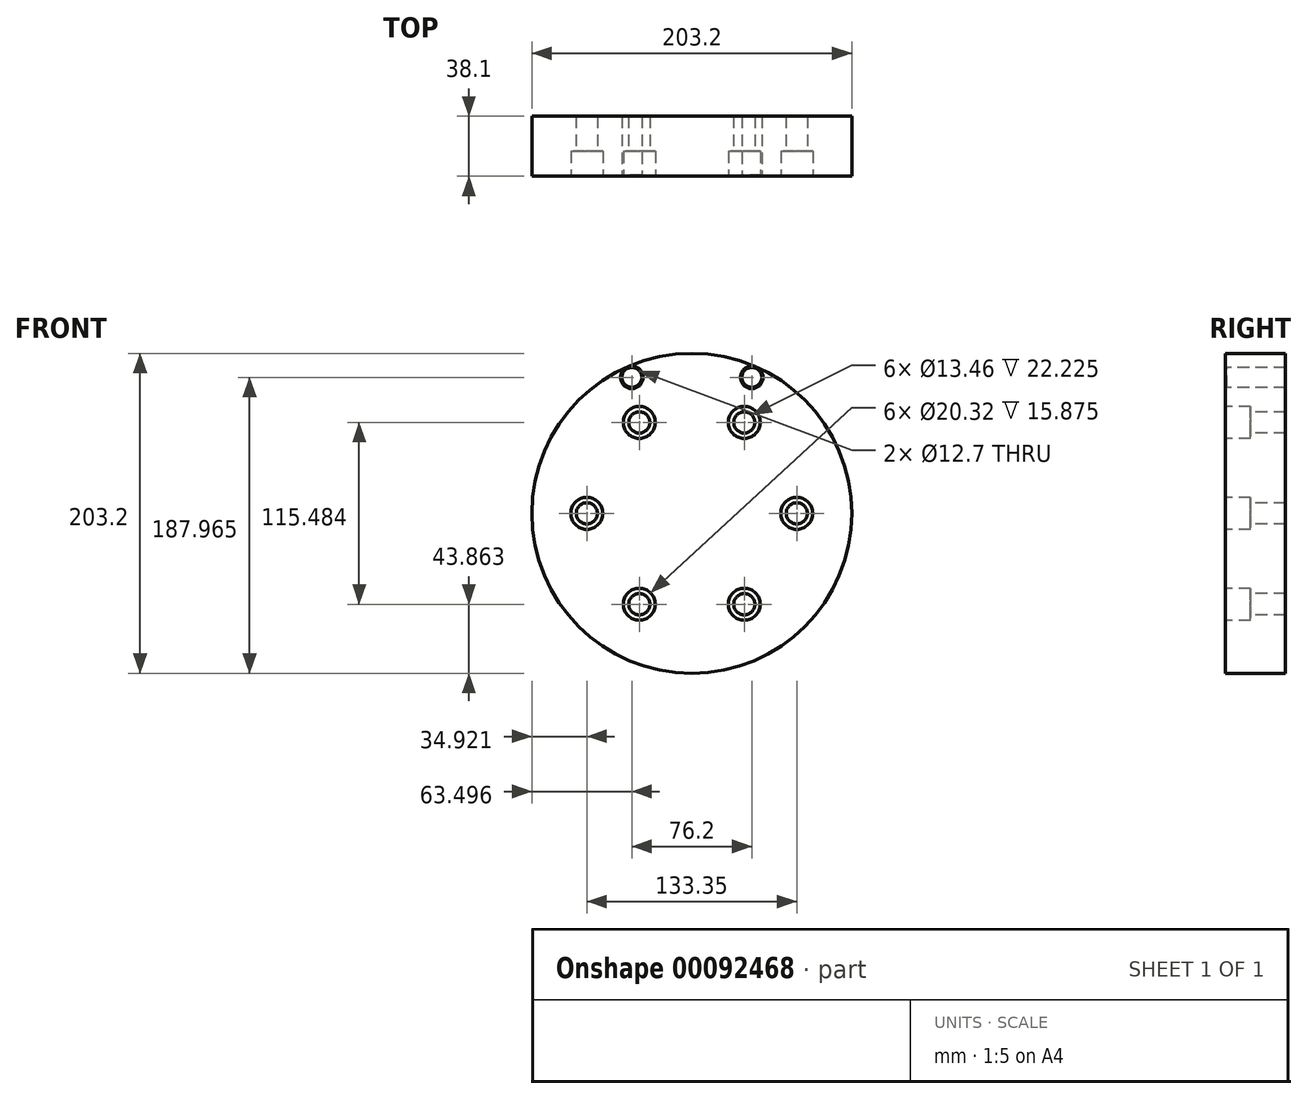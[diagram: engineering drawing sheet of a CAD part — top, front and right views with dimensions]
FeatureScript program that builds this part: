
annotation { "Feature Type Name" : "Feature", "Feature Type Description" : "" }
export const myFeature = defineFeature(function(context is Context, id is Id, definition is map)
    precondition{}
    {
        {
            var Q0;
            Q0=qCreatedBy(makeId("Front.planeOp"),FACE);
            var sketch = newSketch(context, id + "F0", { "sketchPlane" : qUnion([Q0])});
            skCircle(sketch, "E0", {"center": v(0, 0) * mm, "radius": 101.6 * mm});
            skPoint(sketch, "E1", {"position": v(0, 66.68) * mm});
            skPoint(sketch, "E2.1.0", {"position": v(-57.74, 33.34) * mm});
            skPoint(sketch, "E2.2.0", {"position": v(-57.74, -33.34) * mm});
            skPoint(sketch, "E2.3.0", {"position": v(0, -66.68) * mm});
            skPoint(sketch, "E2.4.0", {"position": v(57.74, -33.34) * mm});
            skPoint(sketch, "E2.5.0", {"position": v(57.74, 33.34) * mm});
            skPoint(sketch, "E3", {"position": v(0, 76.2) * mm});
            skCircle(sketch, "E4", {"center": v(-846.13, -154.24) * mm, "radius": 101.6 * mm});
            skCircle(sketch, "E5", {"center": v(-808.03, -67.88) * mm, "radius": 6.53 * mm});
            skCircle(sketch, "E6", {"center": v(-884.23, -67.88) * mm, "radius": 6.53 * mm});
            skSolve(sketch);
        }
        {
            var Q0;
            Q0=makeQuery(id+"F0.imprint","IMPRINT",FACE,{"disambiguationData":[TD([[makeQuery(id+"F0.imprint","IMPRINT",EDGE,{"derivedFrom":sQuery(id+"F0.wireOp",EDGE,"E0")}),1.0]])]});
            var Q1;
            {var subQ0=sQuery(id+"F0.wireOp",EDGE,"aQM3ETqN-wsyi-kC2x-n212-KJofOytAtcY7");var subQ14=sQuery(id+"F0.wireOp",EDGE,"JE2JmhDc-oCCf-cZhW-Kxyp-TygjBwpqUF1L");var subQ17=makeQuery(id+"F0.imprint","INTERSECT",VERTEX,{"disambiguationData":[OD(0.0)],"derivedFrom":[subQ14,subQ0]});Q1=makeQuery(id+"F0.imprint","IMPRINT",FACE,{"disambiguationData":[TD([[makeQuery(id+"F0.imprint","IMPRINT",EDGE,{"disambiguationData":[TD([[subQ17,1.0]])],"derivedFrom":subQ14}),-1.0]])]});}
            extrude(context, id + "F1", {"entities" : qUnion([Q0, Q1]), "oppositeDirection" : true, "depth" : 38.1 * mm});
        }
        {
            var Q0;
            Q0=sQuery(id+"F0.wireOp",VERTEX,"E1");
            var Q1;
            Q1=makeQuery(id+"F1.opExtrude","SWEPT_BODY",BODY,{"disambiguationData":[OSD([sQuery(id+"F0.wireOp",EDGE,"E0")])]});
            hole(context, id + "F2", {"style" : HoleStyle.C_BORE, "endStyle" : HoleEndStyle.BLIND, "holeDiameter" : 13.46 * mm, "cBoreDiameter" : 20.32 * mm, "cBoreDepth" : 15.88 * mm, "holeDepth" : 50.8 * mm, "startFromSketch" : true, "locations" : qUnion([Q0]), "scope" : qUnion([Q1])});
        }
        {
            var Q0;
            Q0=sQuery(id+"F0.wireOp",VERTEX,"E2.1.0");
            var Q1;
            Q1=sQuery(id+"F0.wireOp",VERTEX,"E2.2.0");
            var Q2;
            Q2=sQuery(id+"F0.wireOp",VERTEX,"E2.3.0");
            var Q3;
            Q3=sQuery(id+"F0.wireOp",VERTEX,"E2.4.0");
            var Q4;
            Q4=sQuery(id+"F0.wireOp",VERTEX,"E2.5.0");
            var Q5;
            Q5=makeQuery(id+"F1.opExtrude","SWEPT_BODY",BODY,{"disambiguationData":[OSD([sQuery(id+"F0.wireOp",EDGE,"E0")])]});
            hole(context, id + "F3", {"style" : HoleStyle.C_BORE, "endStyle" : HoleEndStyle.BLIND, "holeDiameter" : 13.46 * mm, "cBoreDiameter" : 20.32 * mm, "cBoreDepth" : 15.88 * mm, "holeDepth" : 50.8 * mm, "startFromSketch" : true, "locations" : qUnion([Q0, Q1, Q2, Q3, Q4]), "scope" : qUnion([Q5])});
        }
        {
            var Q0;
            Q0=makeQuery(id+"F1.opExtrude","SWEPT_BODY",BODY,{"disambiguationData":[OSD([sQuery(id+"F0.wireOp",EDGE,"E0")])]});
            var Q1;
            Q1=sQuery(id+"F0.wireOp",EDGE,"E0");
            transform(context, id + "F4", {"entities" : qUnion([Q0]), "transformType" : TransformType.ROTATION, "transformAxis" : qUnion([Q1]), "angle" : 30 * degree, "makeCopy" : false});
        }
        {
            var Q0;
            Q0=makeQuery(id+"F1.opExtrude","SWEPT_BODY",BODY,{"disambiguationData":[OSD([sQuery(id+"F0.wireOp",EDGE,"E0")])]});
            var Q1;
            Q1=sQuery(id+"F0.wireOp",VERTEX,"E0.center");
            var Q2;
            Q2=sQuery(id+"F0.wireOp",VERTEX,"E4.center");
            transform(context, id + "F5", {"entities" : qUnion([Q0]), "transformType" : TransformType.TRANSLATION_ENTITY, "oppositeDirectionEntity" : false, "transformLine" : qUnion([Q1, Q2]), "makeCopy" : false});
        }
        {
            var Q0;
            Q0=sQuery(id+"F0.wireOp",VERTEX,"E6.center");
            var Q1;
            Q1=sQuery(id+"F0.wireOp",VERTEX,"E5.center");
            var Q2;
            Q2=makeQuery(id+"F1.opExtrude","SWEPT_BODY",BODY,{"disambiguationData":[OSD([sQuery(id+"F0.wireOp",EDGE,"E0")])]});
            hole(context, id + "F6", {"style" : HoleStyle.C_SINK, "endStyle" : HoleEndStyle.BLIND, "holeDiameter" : 12.7 * mm, "cSinkDiameter" : 14.29 * mm, "cSinkAngle" : 90 * degree, "holeDepth" : 50.8 * mm, "startFromSketch" : true, "locations" : qUnion([Q0, Q1]), "scope" : qUnion([Q2])});
        }
    });
